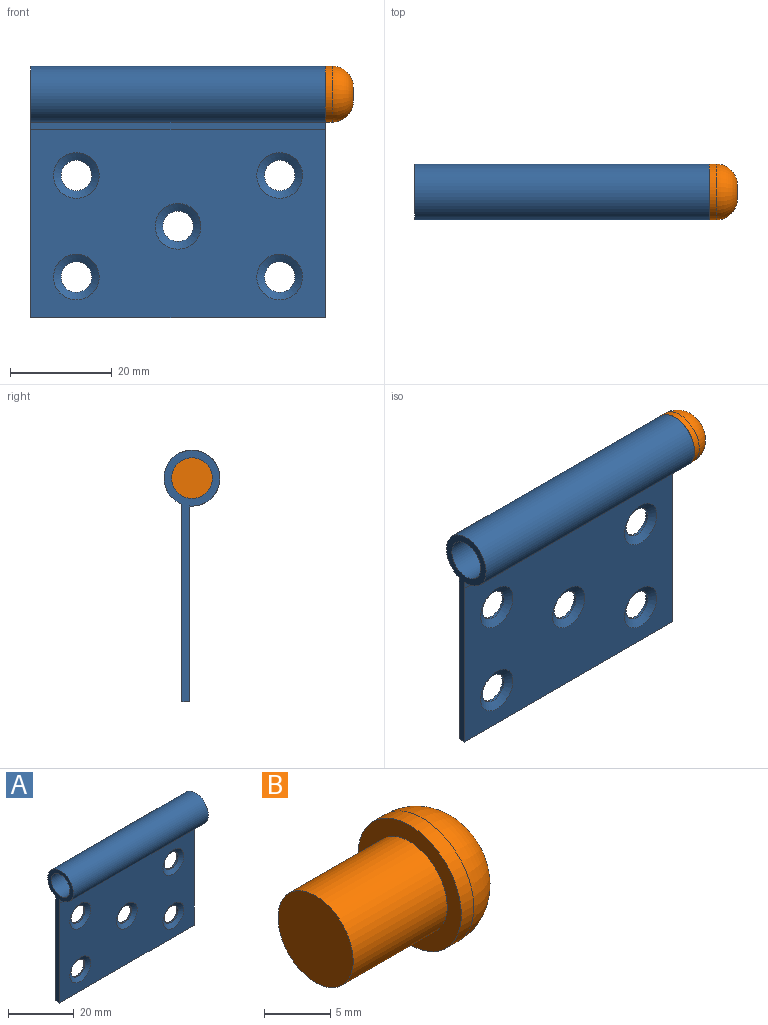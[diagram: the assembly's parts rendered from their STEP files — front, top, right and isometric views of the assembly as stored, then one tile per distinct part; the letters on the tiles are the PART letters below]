
ASSEMBLY  parts=2 mates=1
PART A: 19 faces, bbox 58x11x49.5 mm
  f0: extruded ~58x1.52mm, area 88.3mm2, adj f1,f5,f7,f8
  f1: plane 58x37mm, normal (0,-1,0), area 1827.9mm2, adj f0,f2,f7,f8,f14,f15,f16,f17
  f2: plane 58x1.5mm, normal (0,0,-1), area 87mm2, adj f1,f3,f7,f8
  f3: plane 58x37mm, normal (0,1,0), area 2004.6mm2, adj f2,f4,f7,f8,f9,f10,f11,f12
  f4: extruded ~58x1.87mm, area 108.4mm2, adj f3,f5,f7,f8
  f5: cylinder r=5.5mm len=58mm, axis (-1,0,0), area 1915.4mm2, adj f0,f4,f7,f8
  f6: cylinder r=4mm len=58mm, axis (-1,0,0), area 1457.7mm2, adj f7,f8
  f7: plane 49.5x11mm, normal (1,0,0), area 102.8mm2, adj f0,f1,f2,f3,f4,f5,f6
  f8: plane 49.5x11mm, normal (-1,0,0), area 102.8mm2, adj f0,f1,f2,f3,f4,f5,f6
  f9: cylinder r=3mm len=6mm, axis (0,-1,0), area 9.4mm2, adj f3,f17
  f10: cylinder r=3mm len=6mm, axis (0,-1,0), area 9.4mm2, adj f3,f16
  f11: cylinder r=3mm len=6mm, axis (0,-1,0), area 9.4mm2, adj f3,f14
  f12: cylinder r=3mm len=6mm, axis (0,-1,0), area 9.4mm2, adj f3,f18
  f13: cylinder r=3mm len=6mm, axis (0,-1,0), area 9.4mm2, adj f3,f15
  f14: cone r=3mm half-angle=56.3deg, axis (0,-1,0), area 42.5mm2, adj f1,f11
  f15: cone r=3mm half-angle=56.3deg, axis (0,-1,0), area 42.5mm2, adj f1,f13
  f16: cone r=3mm half-angle=56.3deg, axis (0,-1,0), area 42.5mm2, adj f1,f10
  f17: cone r=3mm half-angle=56.3deg, axis (0,-1,0), area 42.5mm2, adj f1,f9
  f18: cone r=3mm half-angle=56.3deg, axis (0,-1,0), area 42.5mm2, adj f1,f12
PART B: 6 faces, bbox 15.5x11x11 mm
  f0: cylinder r=5.5mm len=11mm, axis (-1,0,0), area 46.1mm2, adj f2,f5
  f1: plane 2.67x2.67mm, normal (1,0,0), area 5.6mm2, adj f5
  f2: plane 11x11mm, normal (-1,0,0), area 44.8mm2, adj f0,f3
  f3: cylinder r=4mm len=10mm, axis (1,0,0), area 251.3mm2, adj f2,f4
  f4: plane 8x8mm, normal (-1,0,0), area 50.3mm2, adj f3
  f5: torus R=1.33mm, axis (1,0,0), area 163.9mm2, adj f0,f1
PLACE A at identity fixed
PLACE B t=(29,0,0)mm
MATE fastened B.f0 <-> A.f5  axis (1,0,0) through (29,-2,184)mm
